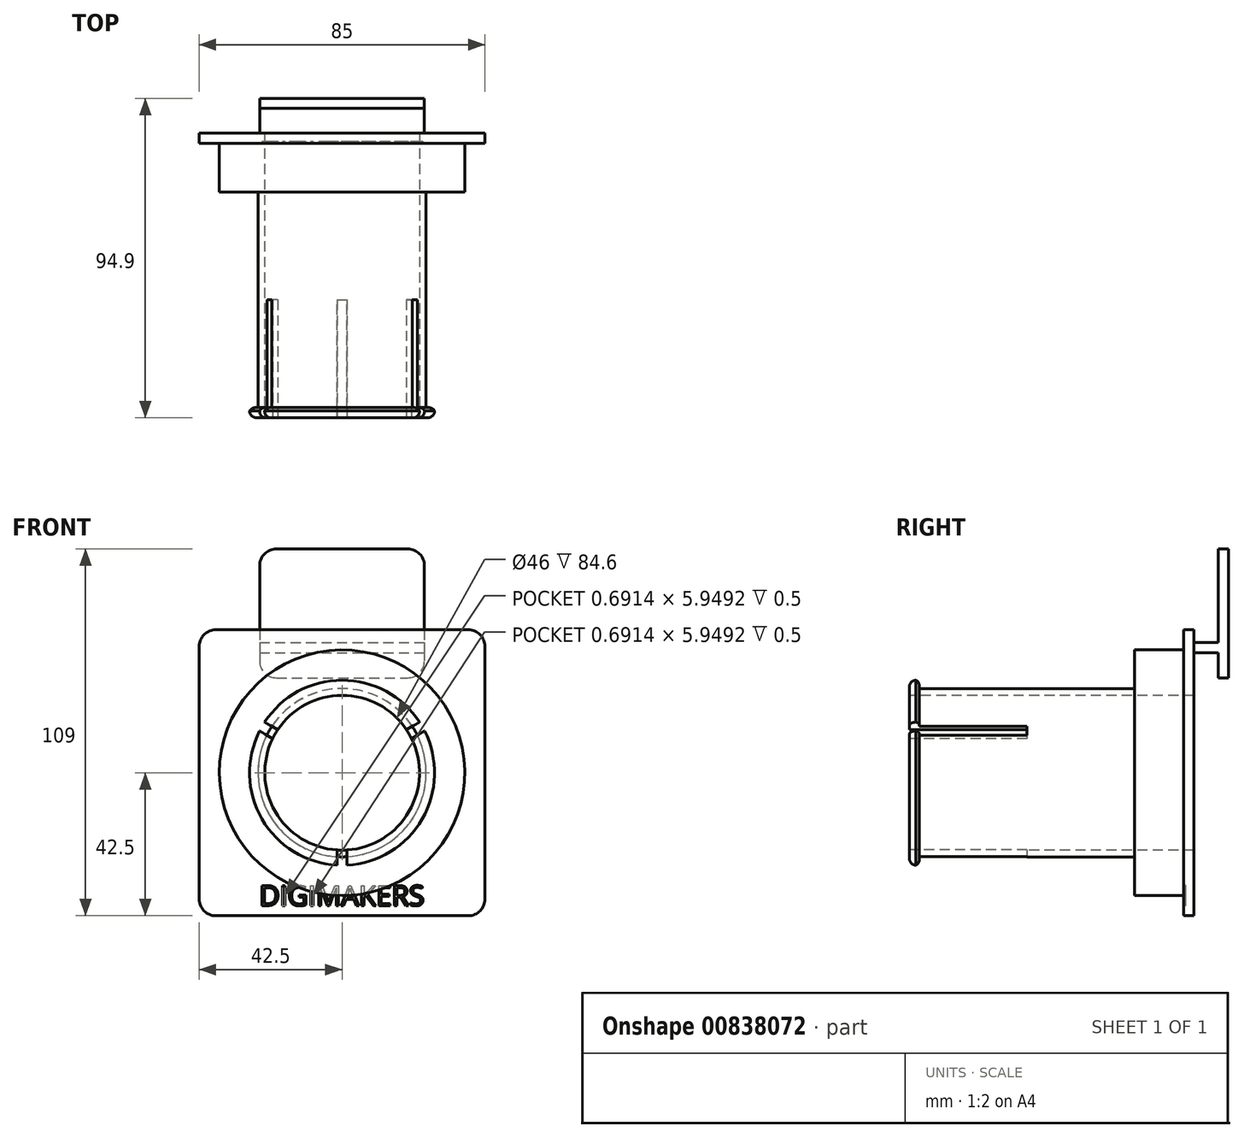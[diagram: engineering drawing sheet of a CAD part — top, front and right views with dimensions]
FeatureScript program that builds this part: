
annotation { "Feature Type Name" : "Feature", "Feature Type Description" : "" }
export const myFeature = defineFeature(function(context is Context, id is Id, definition is map)
    precondition{}
    {
        {
            assignVariable(context, id + "F0", {"name" : "BaseRingHeight", "anyValue" : 0});
        }
        {
            assignVariable(context, id + "F1", {"name" : "SpoolRingHeight", "anyValue" : 64});
        }
        {
            var Q0;
            Q0=qCreatedBy(makeId("Front.planeOp"),FACE);
            var sketch = newSketch(context, id + "F2", { "sketchPlane" : qUnion([Q0])});
            skLineSegment(sketch, "E0.bottom", {"start": v(-44, 38.3) * mm, "end": v(-5, 38.3) * mm});
            skLineSegment(sketch, "E0.top", {"start": v(-44, 0) * mm, "end": v(-5, 0) * mm});
            skLineSegment(sketch, "E0.left", {"start": v(-49, 33.3) * mm, "end": v(-49, 5) * mm});
            skLineSegment(sketch, "E0.right", {"start": v(0, 33.3) * mm, "end": v(0, 5) * mm});
            skPoint(sketch, "E1.visualSharp", {"position": v(-49, 38.3) * mm});
            skArc(sketch, "E1.filletArc", {"start": v(-44, 38.3) * mm, "mid": v(-47.54, 36.84) * mm, "end": v(-49, 33.3) * mm});
            skPoint(sketch, "E2.visualSharp", {"position": v(0, 38.3) * mm});
            skArc(sketch, "E2.filletArc", {"start": v(0, 33.3) * mm, "mid": v(-1.46, 36.84) * mm, "end": v(-5, 38.3) * mm});
            skPoint(sketch, "E3.visualSharp", {"position": v(0, 0) * mm});
            skArc(sketch, "E3.filletArc", {"start": v(-5, 0) * mm, "mid": v(-1.46, 1.46) * mm, "end": v(0, 5) * mm});
            skPoint(sketch, "E4.visualSharp", {"position": v(-49, 0) * mm});
            skArc(sketch, "E4.filletArc", {"start": v(-49, 5) * mm, "mid": v(-47.54, 1.46) * mm, "end": v(-44, 0) * mm});
            skSolve(sketch);
        }
        {
            var Q0;
            Q0=qSketchRegion(id+"F2",true);
            extrude(context, id + "F3", {"entities" : qUnion([Q0]), "depth" : 3 * mm, "offsetDistance" : 25 * mm});
        }
        {
            var Q0;
            Q0=makeQuery(id+"F3.opExtrude","CAP_FACE",FACE,{"disambiguationData":[OSD([sQuery(id+"F2.wireOp",EDGE,"E0.bottom"),sQuery(id+"F2.wireOp",EDGE,"E0.top"),sQuery(id+"F2.wireOp",EDGE,"E0.left"),sQuery(id+"F2.wireOp",EDGE,"E0.right")])],"isStart":false});
            var sketch = newSketch(context, id + "F4", { "sketchPlane" : qUnion([Q0])});
            skLineSegment(sketch, "E5.bottom", {"start": v(-49, 10.5) * mm, "end": v(0, 10.5) * mm});
            skLineSegment(sketch, "E5.top", {"start": v(-49, 7.5) * mm, "end": v(0, 7.5) * mm});
            skLineSegment(sketch, "E5.left", {"start": v(-49, 10.5) * mm, "end": v(-49, 7.5) * mm});
            skLineSegment(sketch, "E5.right", {"start": v(0, 10.5) * mm, "end": v(0, 7.5) * mm});
            skSolve(sketch);
        }
        {
            var Q0;
            Q0=qSketchRegion(id+"F4",true);
            extrude(context, id + "F5", {"entities" : qUnion([Q0]), "operationType" : NewBodyOperationType.ADD, "depth" : 7.3 * mm, "offsetDistance" : 25 * mm});
        }
        {
            var Q0;
            Q0=makeQuery(id+"F5.opExtrude","CAP_FACE",FACE,{"disambiguationData":[OSD([sQuery(id+"F4.wireOp",EDGE,"E5.bottom"),sQuery(id+"F4.wireOp",EDGE,"E5.top"),sQuery(id+"F4.wireOp",EDGE,"E5.left"),sQuery(id+"F4.wireOp",EDGE,"E5.right")])],"isStart":false});
            var sketch = newSketch(context, id + "F6", { "sketchPlane" : qUnion([Q0])});
            skLineSegment(sketch, "E6.bottom", {"start": v(-62, 14.3) * mm, "end": v(13, 14.3) * mm});
            skLineSegment(sketch, "E6.top", {"start": v(-62, -70.7) * mm, "end": v(13, -70.7) * mm});
            skLineSegment(sketch, "E6.left", {"start": v(-67, 9.3) * mm, "end": v(-67, -65.7) * mm});
            skLineSegment(sketch, "E6.right", {"start": v(18, 9.3) * mm, "end": v(18, -65.7) * mm});
            skPoint(sketch, "E7.visualSharp", {"position": v(-67, 14.3) * mm});
            skArc(sketch, "E7.filletArc", {"start": v(-62, 14.3) * mm, "mid": v(-65.54, 12.84) * mm, "end": v(-67, 9.3) * mm});
            skPoint(sketch, "E8.visualSharp", {"position": v(18, 14.3) * mm});
            skArc(sketch, "E8.filletArc", {"start": v(18, 9.3) * mm, "mid": v(16.54, 12.84) * mm, "end": v(13, 14.3) * mm});
            skPoint(sketch, "E9.visualSharp", {"position": v(18, -70.7) * mm});
            skArc(sketch, "E9.filletArc", {"start": v(13, -70.7) * mm, "mid": v(16.54, -69.24) * mm, "end": v(18, -65.7) * mm});
            skPoint(sketch, "E10.visualSharp", {"position": v(-67, -70.7) * mm});
            skArc(sketch, "E10.filletArc", {"start": v(-67, -65.7) * mm, "mid": v(-65.54, -69.24) * mm, "end": v(-62, -70.7) * mm});
            skSolve(sketch);
        }
        {
            var Q0;
            Q0=qSketchRegion(id+"F6",true);
            extrude(context, id + "F7", {"entities" : qUnion([Q0]), "operationType" : NewBodyOperationType.ADD, "depth" : 3 * mm, "offsetDistance" : 25 * mm});
        }
        {
            var Q0;
            Q0=makeQuery(id+"F7.opExtrude","CAP_FACE",FACE,{"disambiguationData":[OSD([sQuery(id+"F6.wireOp",EDGE,"E6.bottom"),sQuery(id+"F6.wireOp",EDGE,"E6.top"),sQuery(id+"F6.wireOp",EDGE,"E6.left"),sQuery(id+"F6.wireOp",EDGE,"E6.right"),sQuery(id+"F6.wireOp",EDGE,"E7.filletArc"),sQuery(id+"F6.wireOp",EDGE,"E8.filletArc"),sQuery(id+"F6.wireOp",EDGE,"E9.filletArc"),sQuery(id+"F6.wireOp",EDGE,"E10.filletArc")])],"isStart":false});
            var sketch = newSketch(context, id + "F8", { "sketchPlane" : qUnion([Q0])});
            skCircle(sketch, "E11", {"center": v(-24.5, -28.2) * mm, "radius": 36.5 * mm});
            skLineSegment(sketch, "E12", {"start": v(-82.43, -28.2) * mm, "end": v(118.43, -28.2) * mm, "construction": true});
            skLineSegment(sketch, "E13", {"start": v(-24.5, 43.68) * mm, "end": v(-24.5, -185.08) * mm, "construction": true});
            skSolve(sketch);
        }
        {
            var Q0;
            Q0=qSketchRegion(id+"F8",true);
            extrude(context, id + "F9", {"entities" : qUnion([Q0]), "operationType" : NewBodyOperationType.ADD, "depth" : (getVariable(context, 'BaseRingHeight') + 14.6) * mm, "offsetDistance" : 25 * mm});
        }
        {
            var Q0;
            Q0=makeQuery(id+"F9.opExtrude","CAP_FACE",FACE,{"disambiguationData":[OSD([sQuery(id+"F8.wireOp",EDGE,"E11")])],"isStart":false});
            var sketch = newSketch(context, id + "F10", { "sketchPlane" : qUnion([Q0])});
            skCircle(sketch, "E14", {"center": v(-24.5, -28.2) * mm, "radius": 25 * mm});
            skSolve(sketch);
        }
        {
            var Q0;
            Q0=qSketchRegion(id+"F10",true);
            var Q1;
            Q1=qSketchRegion(id+"F12",true);
            extrude(context, id + "F11", {"entities" : qUnion([Q0, Q1]), "operationType" : NewBodyOperationType.ADD, "depth" : (getVariable(context, 'SpoolRingHeight')) * mm, "offsetDistance" : 25 * mm});
        }
        {
            var Q0;
            Q0=makeQuery(id+"F11.opExtrude","CAP_FACE",FACE,{"disambiguationData":[OSD([sQuery(id+"F10.wireOp",EDGE,"E14")])],"isStart":false});
            var sketch = newSketch(context, id + "F12", { "sketchPlane" : qUnion([Q0])});
            skCircle(sketch, "E15", {"center": v(-24.5, -28.2) * mm, "radius": 23 * mm});
            skSolve(sketch);
        }
        {
            var Q0;
            Q0=qSketchRegion(id+"F12",true);
            var Q1;
            Q1=makeQuery(id+"F7.opExtrude","CAP_FACE",FACE,{"disambiguationData":[OSD([sQuery(id+"F6.wireOp",EDGE,"E6.bottom"),sQuery(id+"F6.wireOp",EDGE,"E6.top"),sQuery(id+"F6.wireOp",EDGE,"E6.left"),sQuery(id+"F6.wireOp",EDGE,"E6.right"),sQuery(id+"F6.wireOp",EDGE,"E7.filletArc"),sQuery(id+"F6.wireOp",EDGE,"E8.filletArc"),sQuery(id+"F6.wireOp",EDGE,"E9.filletArc"),sQuery(id+"F6.wireOp",EDGE,"E10.filletArc")])],"isStart":true});
            extrude(context, id + "F13", {"entities" : qUnion([Q0]), "operationType" : NewBodyOperationType.REMOVE, "endBound" : BoundingType.UP_TO_SURFACE, "oppositeDirection" : true, "depth" : 25 * mm, "endBoundEntityFace" : qUnion([Q1]), "offsetDistance" : 25 * mm});
        }
        {
            var Q0;
            {var subQ0=sQuery(id+"F10.wireOp",EDGE,"E14");Q0=makeQuery(id+"F17.boolean.opBoolean","SPLIT",FACE,{"disambiguationData":[TD([makeQuery(id+"F17.opExtrude","SWEPT_FACE",FACE,{"disambiguationData":[OSD([sQuery(id+"F16.wireOp",EDGE,"E21.left")])]})])],"derivedFrom":makeQuery(id+"F11.opExtrude","CAP_FACE",FACE,{"disambiguationData":[OSD([subQ0])],"isStart":false})});}
            var sketch = newSketch(context, id + "F14", { "sketchPlane" : qUnion([Q0])});
            skCircle(sketch, "E16", {"center": v(-24.5, -28.2) * mm, "radius": 23 * mm});
            skCircle(sketch, "E17", {"center": v(-24.5, -28.2) * mm, "radius": 27.5 * mm});
            skSolve(sketch);
        }
        {
            var Q0;
            Q0=qSketchRegion(id+"F14",true);
            extrude(context, id + "F15", {"entities" : qUnion([Q0]), "operationType" : NewBodyOperationType.ADD, "depth" : 3 * mm, "offsetDistance" : 25 * mm});
        }
        {
            var Q0;
            Q0=makeQuery(id+"F15.opExtrude","CAP_FACE",FACE,{"disambiguationData":[OSD([sQuery(id+"F14.wireOp",EDGE,"E16"),sQuery(id+"F14.wireOp",EDGE,"E17")])],"isStart":false});
            var sketch = newSketch(context, id + "F16", { "sketchPlane" : qUnion([Q0])});
            skLineSegment(sketch, "E18", {"start": v(-24.5, -28.2) * mm, "end": v(-51, -12.9) * mm, "construction": true});
            skLineSegment(sketch, "E19", {"start": v(-24.5, -28.2) * mm, "end": v(2, -12.9) * mm, "construction": true});
            skLineSegment(sketch, "E20", {"start": v(-24.5, -28.2) * mm, "end": v(-24.5, -58.8) * mm, "construction": true});
            skLineSegment(sketch, "E21.bottom", {"start": v(-26, -28.2) * mm, "end": v(-23, -28.2) * mm});
            skLineSegment(sketch, "E21.top", {"start": v(-26, -58.76) * mm, "end": v(-23, -58.76) * mm});
            skLineSegment(sketch, "E21.left", {"start": v(-26, -28.2) * mm, "end": v(-26, -58.76) * mm});
            skLineSegment(sketch, "E21.right", {"start": v(-23, -28.2) * mm, "end": v(-23, -58.76) * mm});
            skCircle(sketch, "E22", {"center": v(-24.5, -28.2) * mm, "radius": 30.6 * mm, "construction": true});
            skLineSegment(sketch, "E23", {"start": v(1.22, -11.62) * mm, "end": v(2.72, -14.22) * mm});
            skLineSegment(sketch, "E24", {"start": v(2.72, -14.22) * mm, "end": v(-23.75, -29.5) * mm});
            skLineSegment(sketch, "E25", {"start": v(-23.75, -29.5) * mm, "end": v(-25.25, -26.9) * mm});
            skLineSegment(sketch, "E26", {"start": v(-25.25, -26.9) * mm, "end": v(1.22, -11.62) * mm});
            skLineSegment(sketch, "E27", {"start": v(-50.22, -11.62) * mm, "end": v(-51.72, -14.22) * mm});
            skLineSegment(sketch, "E28", {"start": v(-51.72, -14.22) * mm, "end": v(-25.25, -29.5) * mm});
            skLineSegment(sketch, "E29", {"start": v(-25.25, -29.5) * mm, "end": v(-23.75, -26.9) * mm});
            skLineSegment(sketch, "E30", {"start": v(-23.75, -26.9) * mm, "end": v(-50.22, -11.62) * mm});
            skSolve(sketch);
        }
        {
            var Q0;
            Q0=qSketchRegion(id+"F16",true);
            extrude(context, id + "F17", {"entities" : qUnion([Q0]), "operationType" : NewBodyOperationType.REMOVE, "oppositeDirection" : true, "depth" : 70 * mm, "offsetDistance" : 25 * mm, "symmetric" : true});
        }
        {
            var Q0;
            {var subQ0=sQuery(id+"F14.wireOp",EDGE,"E17");Q0=makeQuery(id+"F17.boolean.opBoolean","SPLIT",EDGE,{"disambiguationData":[TD([makeQuery(id+"F17.opExtrude","SWEPT_FACE",FACE,{"disambiguationData":[OSD([sQuery(id+"F16.wireOp",EDGE,"E21.left")])]})])],"derivedFrom":makeQuery(id+"F15.opExtrude","CAP_EDGE",EDGE,{"disambiguationData":[OSD([subQ0])],"isStart":false})});}
            var Q1;
            {var subQ0=sQuery(id+"F14.wireOp",EDGE,"E17");Q1=makeQuery(id+"F17.boolean.opBoolean","SPLIT",EDGE,{"disambiguationData":[TD([makeQuery(id+"F17.opExtrude","SWEPT_FACE",FACE,{"disambiguationData":[OSD([sQuery(id+"F16.wireOp",EDGE,"E26")])]})])],"derivedFrom":makeQuery(id+"F15.opExtrude","CAP_EDGE",EDGE,{"disambiguationData":[OSD([subQ0])],"isStart":false})});}
            var Q2;
            {var subQ0=sQuery(id+"F14.wireOp",EDGE,"E17");Q2=makeQuery(id+"F17.boolean.opBoolean","SPLIT",EDGE,{"disambiguationData":[TD([makeQuery(id+"F17.opExtrude","SWEPT_FACE",FACE,{"disambiguationData":[OSD([sQuery(id+"F16.wireOp",EDGE,"E21.right")])]})])],"derivedFrom":makeQuery(id+"F15.opExtrude","CAP_EDGE",EDGE,{"disambiguationData":[OSD([subQ0])],"isStart":false})});}
            fillet(context, id + "F18", {"entities" : qUnion([Q0, Q1, Q2]), "radius" : 2 * mm, "tangentPropagation" : true, "allowEdgeOverflow" : false});
        }
        {
            var Q0;
            {var subQ0=sQuery(id+"F14.wireOp",EDGE,"E17");Q0=makeQuery(id+"F17.boolean.opBoolean","SPLIT",EDGE,{"disambiguationData":[TD([makeQuery(id+"F17.opExtrude","SWEPT_FACE",FACE,{"disambiguationData":[OSD([sQuery(id+"F16.wireOp",EDGE,"E21.right")])]})])],"derivedFrom":makeQuery(id+"F15.opExtrude","CAP_EDGE",EDGE,{"disambiguationData":[OSD([subQ0])],"isStart":true})});}
            var Q1;
            {var subQ0=sQuery(id+"F14.wireOp",EDGE,"E17");Q1=makeQuery(id+"F17.boolean.opBoolean","SPLIT",EDGE,{"disambiguationData":[TD([makeQuery(id+"F17.opExtrude","SWEPT_FACE",FACE,{"disambiguationData":[OSD([sQuery(id+"F16.wireOp",EDGE,"E26")])]})])],"derivedFrom":makeQuery(id+"F15.opExtrude","CAP_EDGE",EDGE,{"disambiguationData":[OSD([subQ0])],"isStart":true})});}
            var Q2;
            {var subQ0=sQuery(id+"F14.wireOp",EDGE,"E17");Q2=makeQuery(id+"F17.boolean.opBoolean","SPLIT",EDGE,{"disambiguationData":[TD([makeQuery(id+"F17.opExtrude","SWEPT_FACE",FACE,{"disambiguationData":[OSD([sQuery(id+"F16.wireOp",EDGE,"E21.left")])]})])],"derivedFrom":makeQuery(id+"F15.opExtrude","CAP_EDGE",EDGE,{"disambiguationData":[OSD([subQ0])],"isStart":true})});}
            fillet(context, id + "F19", {"entities" : qUnion([Q0, Q1, Q2]), "radius" : 2 * mm, "tangentPropagation" : true, "allowEdgeOverflow" : false});
        }
        {
            var Q0;
            Q0=makeQuery(id+"F8.imprint","IMPRINT",FACE,{"disambiguationData":[TD([[makeQuery(id+"F8.imprint","IMPRINT",EDGE,{"derivedFrom":sQuery(id+"F8.wireOp",EDGE,"E11")}),-1.0]])]});
            var sketch = newSketch(context, id + "F20", { "sketchPlane" : qUnion([Q0])});
            skText(sketch, "E31", { "text": "DIGIMAKERS", "fontName": "OpenSans-Regular.ttf"});
            skLineSegment(sketch, "E32", {"start": v(14.01, -67.7) * mm, "end": v(-56.31, -67.7) * mm, "construction": true});
            const initialGuessF20  = {"E31": [-0.0491, -0.0677, 1, 0, 0.006]};
            skSetInitialGuess(sketch, initialGuessF20);
            skSolve(sketch);
        }
        {
            var Q0;
            Q0=qSketchRegion(id+"F20",true);
            extrude(context, id + "F21", {"entities" : qUnion([Q0]), "operationType" : NewBodyOperationType.REMOVE, "oppositeDirection" : true, "depth" : .5 * mm, "offsetDistance" : 25 * mm});
        }
    });
